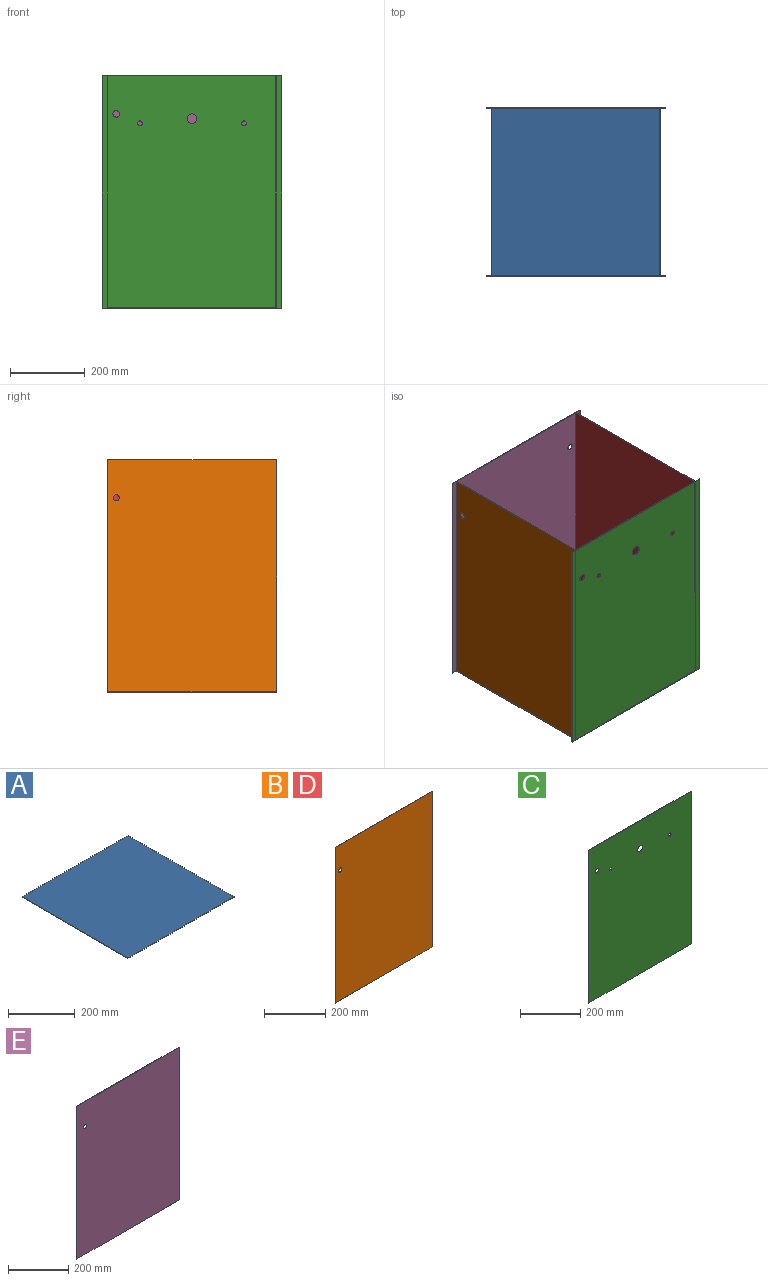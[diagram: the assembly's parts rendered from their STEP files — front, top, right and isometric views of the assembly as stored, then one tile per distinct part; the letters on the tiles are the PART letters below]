
ASSEMBLY  parts=5 mates=11
PART A: 6 faces, bbox 450.9x450.9x1.6 mm
  f0: plane 450.85x1.59mm, normal (0,1,0), area 715.7mm2, adj f1,f3,f4,f5
  f1: plane 450.85x1.59mm, normal (-1,0,0), area 715.7mm2, adj f0,f2,f4,f5
  f2: plane 450.85x1.59mm, normal (0,-1,0), area 715.7mm2, adj f1,f3,f4,f5
  f3: plane 450.85x1.59mm, normal (1,0,0), area 715.7mm2, adj f0,f2,f4,f5
  f4: plane 450.85x450.85mm, normal (0,0,1), area 203265.7mm2, adj f0,f1,f2,f3
  f5: plane 450.85x450.85mm, normal (0,0,-1), area 203265.7mm2, adj f0,f1,f2,f3
PART B: 7 faces, bbox 450.9x1.6x622.3 mm
  f0: plane 450.85x1.59mm, normal (0,0,1), area 715.7mm2, adj f1,f4,f5,f6
  f1: plane 622.3x1.59mm, normal (-1,0,0), area 987.9mm2, adj f0,f2,f5,f6
  f2: plane 450.85x1.59mm, normal (0,0,-1), area 715.7mm2, adj f1,f4,f5,f6
  f3: cylinder r=8.26mm len=16.51mm, axis (0,1,0), area 82.3mm2, adj f5,f6
  f4: plane 622.3x1.59mm, normal (1,0,0), area 987.9mm2, adj f0,f2,f5,f6
  f5: plane 622.3x450.85mm, normal (0,-1,0), area 280349.9mm2, adj f0,f1,f2,f3,f4
  f6: plane 622.3x450.85mm, normal (0,1,0), area 280349.9mm2, adj f0,f1,f2,f3,f4
PART C: 10 faces, bbox 482.6x1.6x622.3 mm
  f0: plane 482.6x1.59mm, normal (0,0,1), area 766.1mm2, adj f1,f7,f8,f9
  f1: plane 622.3x1.59mm, normal (-1,0,0), area 987.9mm2, adj f0,f2,f8,f9
  f2: plane 482.6x1.59mm, normal (0,0,-1), area 766.1mm2, adj f1,f7,f8,f9
  f3: cylinder r=12.7mm len=25.4mm, axis (0,1,0), area 126.7mm2, adj f8,f9
  f4: cylinder r=6.35mm len=12.7mm, axis (0,1,0), area 63.3mm2, adj f8,f9
  f5: cylinder r=6.35mm len=12.7mm, axis (0,1,0), area 63.3mm2, adj f8,f9
  f6: cylinder r=8.92mm len=17.83mm, axis (0,1,0), area 88.9mm2, adj f8,f9
  f7: plane 622.3x1.59mm, normal (1,0,0), area 987.9mm2, adj f0,f2,f8,f9
  f8: plane 622.3x482.6mm, normal (0,-1,0), area 299312.2mm2, adj f0,f1,f2,f3,f4,f5,f6,f7
  f9: plane 622.3x482.6mm, normal (0,1,0), area 299312.2mm2, adj f0,f1,f2,f3,f4,f5,f6,f7
PART D: same geometry as B
PART E: 7 faces, bbox 482.6x1.6x622.3 mm
  f0: plane 482.6x1.59mm, normal (0,0,1), area 766.1mm2, adj f1,f4,f5,f6
  f1: plane 622.3x1.59mm, normal (-1,0,0), area 987.9mm2, adj f0,f2,f5,f6
  f2: plane 482.6x1.59mm, normal (0,0,-1), area 766.1mm2, adj f1,f4,f5,f6
  f3: cylinder r=8.26mm len=16.51mm, axis (0,1,0), area 82.3mm2, adj f5,f6
  f4: plane 622.3x1.59mm, normal (1,0,0), area 987.9mm2, adj f0,f2,f5,f6
  f5: plane 622.3x482.6mm, normal (0,-1,0), area 300107.9mm2, adj f0,f1,f2,f3,f4
  f6: plane 622.3x482.6mm, normal (0,1,0), area 300107.9mm2, adj f0,f1,f2,f3,f4
PLACE A t=(-185.1,-569.22,-822.59)mm
PLACE B rot(axis=(0,0,-1),90deg) t=(-410.52,-569.22,-511.44)mm
PLACE C t=(-184.4,-794.64,-511.44)mm
PLACE D rot(axis=(0,0,1),90deg) t=(40.33,-569.22,-511.44)mm
PLACE E rot(axis=(0,0,1),180deg) t=(-184.4,-343.79,-511.44)mm
MATE planar B.f1 <-> E.f6  axis (0,1,0) through (-411.32,-343.79,-511.44)mm
MATE planar D.f4 <-> E.f6  axis (0,1,0) through (41.12,-343.79,-511.44)mm
MATE planar E.f0 <-> D.f0  axis (0,0,1) through (-184.4,-343,-200.29)mm
MATE planar D.f6 <-> A.f3  axis (-1,0,0) through (40.33,-569.06,-511.6)mm
MATE planar B.f0 <-> C.f0  axis (0,0,1) through (-411.32,-569.22,-200.29)mm
MATE planar D.f0 <-> C.f0  axis (0,0,1) through (41.12,-569.22,-200.29)mm
MATE planar B.f6 <-> A.f1  axis (1,0,0) through (-410.52,-569.37,-511.6)mm
MATE planar A.f5 <-> B.f2  axis (0,0,-1) through (-185.1,-569.22,-822.59)mm
MATE planar B.f4 <-> C.f9  axis (0,-1,0) through (-411.32,-794.64,-511.44)mm
MATE planar C.f9 <-> A.f2  axis (0,1,0) through (-184.23,-794.64,-512.11)mm
MATE planar E.f4 <-> C.f1  axis (-1,0,0) through (-425.7,-343,-511.44)mm
